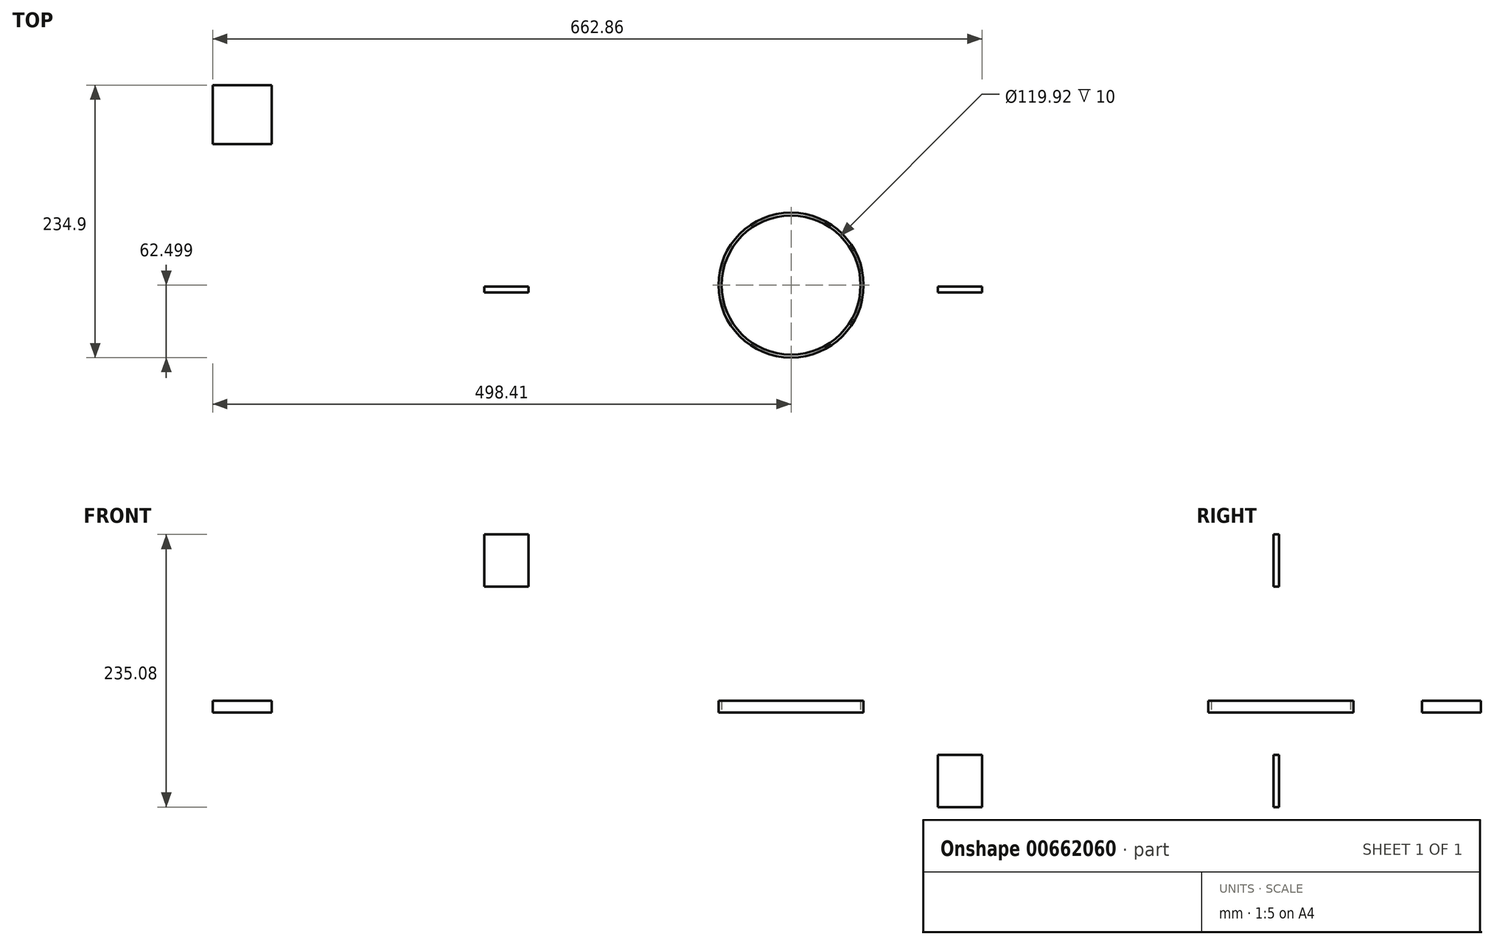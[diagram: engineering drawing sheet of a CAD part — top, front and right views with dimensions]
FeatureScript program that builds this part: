
annotation { "Feature Type Name" : "Feature", "Feature Type Description" : "" }
export const myFeature = defineFeature(function(context is Context, id is Id, definition is map)
    precondition{}
    {
        {
            var Q0;
            Q0=qCreatedBy(makeId("Top.planeOp"),FACE);
            var sketch = newSketch(context, id + "F0", { "sketchPlane" : qUnion([Q0])});
            skCircle(sketch, "E0", {"center": v(1.29, 1.4) * mm, "radius": 62.5 * mm});
            skLineSegment(sketch, "E1.bottom", {"start": v(11.87, -53.1) * mm, "end": v(31.86, -53.1) * mm});
            skLineSegment(sketch, "E1.top", {"start": v(11.87, -116.6) * mm, "end": v(31.86, -116.6) * mm});
            skLineSegment(sketch, "E1.left", {"start": v(11.87, -53.1) * mm, "end": v(11.87, -116.6) * mm});
            skLineSegment(sketch, "E1.right", {"start": v(31.86, -53.1) * mm, "end": v(31.86, -116.6) * mm});
            skLineSegment(sketch, "E2.bottom", {"start": v(-28.12, -53.74) * mm, "end": v(-8.13, -53.74) * mm});
            skLineSegment(sketch, "E2.top", {"start": v(-28.12, -117.24) * mm, "end": v(-8.13, -117.24) * mm});
            skLineSegment(sketch, "E2.left", {"start": v(-28.12, -53.74) * mm, "end": v(-28.12, -117.24) * mm});
            skLineSegment(sketch, "E2.right", {"start": v(-8.13, -53.74) * mm, "end": v(-8.13, -117.24) * mm});
            skLineSegment(sketch, "E3.bottom", {"start": v(-497.12, 173.81) * mm, "end": v(-446.32, 173.81) * mm});
            skLineSegment(sketch, "E3.top", {"start": v(-497.12, 123.01) * mm, "end": v(-446.32, 123.01) * mm});
            skLineSegment(sketch, "E3.left", {"start": v(-497.12, 173.81) * mm, "end": v(-497.12, 123.01) * mm});
            skLineSegment(sketch, "E3.right", {"start": v(-446.32, 173.81) * mm, "end": v(-446.32, 123.01) * mm});
            skSolve(sketch);
        }
        {
            var Q0;
            Q0=makeQuery(id+"F0.imprint","IMPRINT",FACE,{"disambiguationData":[TD([[makeQuery(id+"F0.imprint","IMPRINT",EDGE,{"derivedFrom":sQuery(id+"F0.wireOp",EDGE,"E3.bottom")}),-1.0]])]});
            var Q1;
            {var subQ0=sQuery(id+"F0.wireOp",EDGE,"E2.bottom");Q1=makeQuery(id+"F0.imprint","IMPRINT",FACE,{"disambiguationData":[TD([[makeQuery(id+"F0.imprint","IMPRINT",EDGE,{"derivedFrom":subQ0}),-1.0]])]});}
            var Q2;
            {var subQ0=sQuery(id+"F0.wireOp",EDGE,"E1.bottom");Q2=makeQuery(id+"F0.imprint","IMPRINT",FACE,{"disambiguationData":[TD([[makeQuery(id+"F0.imprint","IMPRINT",EDGE,{"derivedFrom":subQ0}),1.0]])]});}
            var Q3;
            {var subQ0=sQuery(id+"F0.wireOp",EDGE,"E1.bottom");Q3=makeQuery(id+"F0.imprint","IMPRINT",FACE,{"disambiguationData":[TD([[makeQuery(id+"F0.imprint","IMPRINT",EDGE,{"derivedFrom":subQ0}),-1.0]])]});}
            extrude(context, id + "F1", {"entities" : qUnion([Q0, Q1, Q2, Q3]), "depth" : 10 * mm, "offsetDistance" : 25.4 * mm});
        }
        {
            var Q0;
            Q0=qCreatedBy(makeId("Front.planeOp"),FACE);
            var sketch = newSketch(context, id + "F2", { "sketchPlane" : qUnion([Q0])});
            skLineSegment(sketch, "E4.bottom", {"start": v(127.64, -36.48) * mm, "end": v(165.74, -36.48) * mm});
            skLineSegment(sketch, "E4.top", {"start": v(127.64, -81.48) * mm, "end": v(165.74, -81.48) * mm});
            skLineSegment(sketch, "E4.left", {"start": v(127.64, -36.48) * mm, "end": v(127.64, -81.48) * mm});
            skLineSegment(sketch, "E4.right", {"start": v(165.74, -36.48) * mm, "end": v(165.74, -81.48) * mm});
            skLineSegment(sketch, "E5.bottom", {"start": v(-263.04, 153.6) * mm, "end": v(-224.94, 153.6) * mm});
            skLineSegment(sketch, "E5.top", {"start": v(-263.04, 108.6) * mm, "end": v(-224.94, 108.6) * mm});
            skLineSegment(sketch, "E5.left", {"start": v(-263.04, 153.6) * mm, "end": v(-263.04, 108.6) * mm});
            skLineSegment(sketch, "E5.right", {"start": v(-224.94, 153.6) * mm, "end": v(-224.94, 108.6) * mm});
            skSolve(sketch);
        }
        {
            var Q0;
            Q0 = qSketchRegion(id + "F2", true);
            extrude(context, id + "F3", {"entities" : qUnion([Q0]), "depth" : 5 * mm, "offsetDistance" : 25.4 * mm});
        }
        {
            var Q0;
            Q0=makeQuery(id+"F0.imprint","IMPRINT",FACE,{"disambiguationData":[TD([[makeQuery(id+"F0.imprint","IMPRINT",EDGE,{"derivedFrom":sQuery(id+"F0.wireOp",EDGE,"E3.bottom")}),-1.0]])]});
            extrude(context, id + "F4", {"entities" : qUnion([Q0]), "operationType" : NewBodyOperationType.ADD, "depth" : 10 * mm, "offsetDistance" : 25.4 * mm});
        }
        {
            var Q0;
            Q0=makeQuery(id+"F1.opExtrude","CAP_FACE",FACE,{"disambiguationData":[OSD([sQuery(id+"F0.wireOp",EDGE,"E0"),sQuery(id+"F0.wireOp",EDGE,"E1.top"),sQuery(id+"F0.wireOp",EDGE,"E1.left"),sQuery(id+"F0.wireOp",EDGE,"E1.right"),sQuery(id+"F0.wireOp",EDGE,"E2.top"),sQuery(id+"F0.wireOp",EDGE,"E2.left"),sQuery(id+"F0.wireOp",EDGE,"E2.right")])],"isStart":false});
            var Q1;
            Q1=makeQuery(id+"F1.opExtrude","CAP_FACE",FACE,{"disambiguationData":[OSD([sQuery(id+"F0.wireOp",EDGE,"E0"),sQuery(id+"F0.wireOp",EDGE,"E1.top"),sQuery(id+"F0.wireOp",EDGE,"E1.left"),sQuery(id+"F0.wireOp",EDGE,"E1.right"),sQuery(id+"F0.wireOp",EDGE,"E2.top"),sQuery(id+"F0.wireOp",EDGE,"E2.left"),sQuery(id+"F0.wireOp",EDGE,"E2.right")])],"isStart":true});
            shell(context, id + "F5", {"entities" : qUnion([Q0, Q1]), "thickness" : 2.54 * mm});
        }
    });
